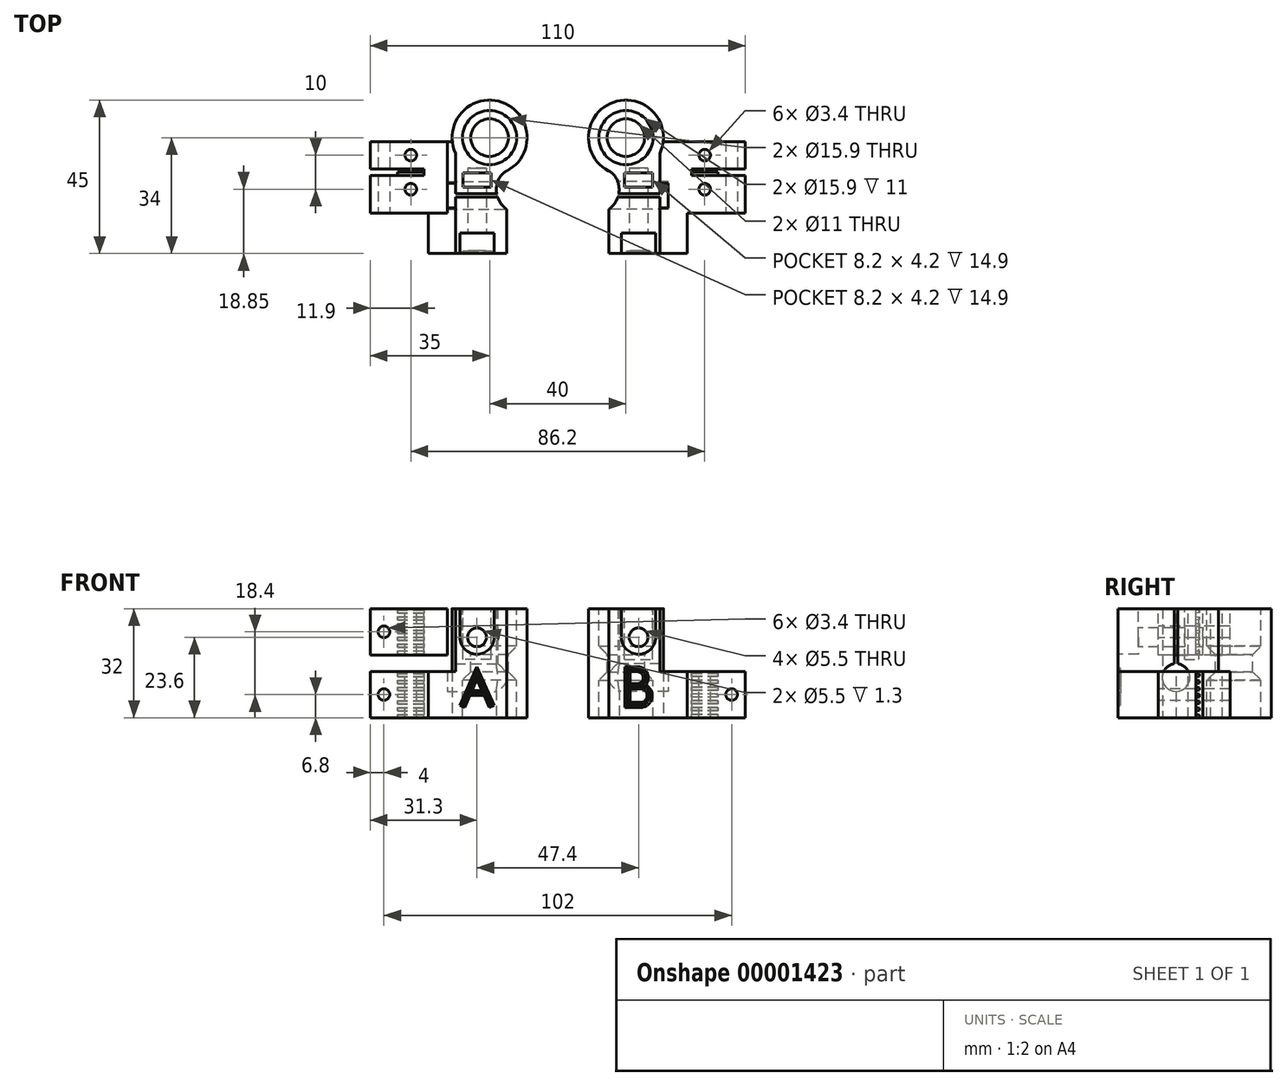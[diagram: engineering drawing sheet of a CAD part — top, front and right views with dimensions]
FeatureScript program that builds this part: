
annotation { "Feature Type Name" : "Feature", "Feature Type Description" : "" }
export const myFeature = defineFeature(function(context is Context, id is Id, definition is map)
    precondition{}
    {
        {
            var Q0;
            Q0=qCreatedBy(makeId("Top.planeOp"),FACE);
            var sketch = newSketch(context, id + "F0", { "sketchPlane" : qUnion([Q0])});
            skArc(sketch, "E0", {"start": v(4.19, -10.17) * mm, "mid": v(5.63, 9.45) * mm, "end": v(-10.94, -1.15) * mm});
            skLineSegment(sketch, "E1", {"start": v(-10.94, -1.15) * mm, "end": v(-35, -1.15) * mm});
            skLineSegment(sketch, "E2", {"start": v(-35, -1.15) * mm, "end": v(-35, -9.15) * mm});
            skLineSegment(sketch, "E3", {"start": v(-35, -9.15) * mm, "end": v(-19.3, -9.15) * mm});
            skLineSegment(sketch, "E4", {"start": v(-19.3, -9.15) * mm, "end": v(-19.3, -11.15) * mm});
            skLineSegment(sketch, "E5", {"start": v(-19.3, -11.15) * mm, "end": v(-35, -11.15) * mm});
            skLineSegment(sketch, "E6", {"start": v(-35, -11.15) * mm, "end": v(-35, -22.15) * mm});
            skLineSegment(sketch, "E7", {"start": v(-35, -22.15) * mm, "end": v(-18, -22.15) * mm});
            skLineSegment(sketch, "E8", {"start": v(-18, -22.15) * mm, "end": v(-18, -34) * mm});
            skLineSegment(sketch, "E9", {"start": v(-18, -34) * mm, "end": v(5, -34) * mm});
            skLineSegment(sketch, "E10", {"start": v(5, -34) * mm, "end": v(5, -21) * mm});
            skArc(sketch, "E11", {"start": v(4.19, -10.17) * mm, "mid": v(2.02, -15.78) * mm, "end": v(5, -21) * mm});
            skSolve(sketch);
        }
        {
            var Q0;
            Q0=makeQuery(id+"F0.imprint","IMPRINT",FACE,{"disambiguationData":[TD([[makeQuery(id+"F0.imprint","IMPRINT",EDGE,{"derivedFrom":sQuery(id+"F0.wireOp",EDGE,"E0")}),1.0]])]});
            extrude(context, id + "F1", {"entities" : qUnion([Q0]), "depth" : 32 * mm});
        }
        {
            var Q0;
            Q0=makeQuery(id+"F1.opExtrude","CAP_FACE",FACE,{"disambiguationData":[OSD([sQuery(id+"F0.wireOp",EDGE,"E0"),sQuery(id+"F0.wireOp",EDGE,"E1"),sQuery(id+"F0.wireOp",EDGE,"E2"),sQuery(id+"F0.wireOp",EDGE,"E3"),sQuery(id+"F0.wireOp",EDGE,"E4"),sQuery(id+"F0.wireOp",EDGE,"E5"),sQuery(id+"F0.wireOp",EDGE,"E6"),sQuery(id+"F0.wireOp",EDGE,"E7"),sQuery(id+"F0.wireOp",EDGE,"E8"),sQuery(id+"F0.wireOp",EDGE,"E9"),sQuery(id+"F0.wireOp",EDGE,"E10"),sQuery(id+"F0.wireOp",EDGE,"E11")])],"isStart":false});
            var sketch = newSketch(context, id + "F2", { "sketchPlane" : qUnion([Q0])});
            skLineSegment(sketch, "E12", {"start": v(-10, -34) * mm, "end": v(-10, -4.58) * mm});
            skArc(sketch, "E13", {"start": v(-10.94, -1.15) * mm, "mid": v(-10.6, -2.9) * mm, "end": v(-10, -4.58) * mm});
            skSolve(sketch);
        }
        {
            var Q0;
            Q0 = qSketchRegion(id + "F2", true);
            var Q1;
            {var subQ1=sQuery(id+"F2.wireOp",EDGE,"E12");Q1=makeQuery(id+"F2.imprint","IMPRINT",FACE,{"disambiguationData":[TD([[makeQuery(id+"F2.imprint","IMPRINT",EDGE,{"derivedFrom":subQ1}),1.0]])]});}
            extrude(context, id + "F3", {"entities" : qUnion([Q0, Q1]), "operationType" : NewBodyOperationType.REMOVE, "oppositeDirection" : true, "depth" : 18.4 * mm});
        }
        {
            var Q0;
            Q0=qCreatedBy(makeId("Front.planeOp"),FACE);
            var sketch = newSketch(context, id + "F4", { "sketchPlane" : qUnion([Q0])});
            skLineSegment(sketch, "E14.0", {"start": v(-11, 32) * mm, "end": v(11, 32) * mm, "construction": true});
            skLineSegment(sketch, "E15.0", {"start": v(-11, 0) * mm, "end": v(11, 0) * mm, "construction": true});
            skLineSegment(sketch, "E16", {"start": v(0, 0) * mm, "end": v(0, 32) * mm});
            skLineSegment(sketch, "E17", {"start": v(0, 32) * mm, "end": v(7.95, 32) * mm, "construction": true});
            skLineSegment(sketch, "E18", {"start": v(7.95, 32) * mm, "end": v(7.95, 21) * mm, "construction": true});
            skLineSegment(sketch, "E19", {"start": v(7.95, 21) * mm, "end": v(5.5, 18.55) * mm, "construction": true});
            skLineSegment(sketch, "E20", {"start": v(5.5, 18.55) * mm, "end": v(5.5, 13.45) * mm, "construction": true});
            skLineSegment(sketch, "E21", {"start": v(5.5, 13.45) * mm, "end": v(7.95, 11) * mm, "construction": true});
            skLineSegment(sketch, "E22", {"start": v(7.95, 11) * mm, "end": v(7.95, 0) * mm, "construction": true});
            skLineSegment(sketch, "E23", {"start": v(7.95, 0) * mm, "end": v(0, 0) * mm, "construction": true});
            skLineSegment(sketch, "E24", {"start": v(-7.95, 0) * mm, "end": v(-7.95, 11) * mm});
            skLineSegment(sketch, "E25", {"start": v(-7.95, 11) * mm, "end": v(-5.5, 13.45) * mm});
            skLineSegment(sketch, "E26", {"start": v(-5.5, 13.45) * mm, "end": v(-5.5, 18.55) * mm});
            skLineSegment(sketch, "E27", {"start": v(-5.5, 18.55) * mm, "end": v(-7.95, 21) * mm});
            skLineSegment(sketch, "E28", {"start": v(-7.95, 21) * mm, "end": v(-7.95, 32) * mm});
            skLineSegment(sketch, "E29", {"start": v(-7.95, 32) * mm, "end": v(0, 32) * mm});
            skLineSegment(sketch, "E30", {"start": v(0, 0) * mm, "end": v(-7.95, 0) * mm});
            skSolve(sketch);
        }
        {
            var Q0;
            Q0=makeQuery(id+"F4.imprint","IMPRINT",FACE,{"disambiguationData":[TD([[makeQuery(id+"F4.imprint","IMPRINT",EDGE,{"derivedFrom":sQuery(id+"F4.wireOp",EDGE,"E16")}),1.0]])]});
            var Q1;
            Q1=sQuery(id+"F4.wireOp",EDGE,"E16");
            revolve(context, id + "F5", {"operationType" : NewBodyOperationType.REMOVE, "entities" : qUnion([Q0]), "axis" : qUnion([Q1]), "revolveType" : RevolveType.FULL, "oppositeDirection" : true});
        }
        {
            var Q0;
            Q0=makeQuery(id+"F1.opExtrude","SWEPT_FACE",FACE,{"disambiguationData":[OSD([sQuery(id+"F0.wireOp",EDGE,"E10")])]});
            var sketch = newSketch(context, id + "F6", { "sketchPlane" : qUnion([Q0])});
            skArc(sketch, "E31", {"start": v(-17.5, 15.82) * mm, "mid": v(-17, 7.75) * mm, "end": v(-16.5, 15.82) * mm});
            skLineSegment(sketch, "E32", {"start": v(-17, 11.8) * mm, "end": v(-17, 32) * mm, "construction": true});
            skLineSegment(sketch, "E33", {"start": v(-17, 32) * mm, "end": v(-17.5, 32) * mm});
            skLineSegment(sketch, "E34", {"start": v(-17.5, 32) * mm, "end": v(-17.5, 15.82) * mm});
            skLineSegment(sketch, "E35", {"start": v(-17.5, 15.82) * mm, "end": v(-16.5, 15.82) * mm, "construction": true});
            skLineSegment(sketch, "E36", {"start": v(-16.5, 15.82) * mm, "end": v(-16.5, 32) * mm});
            skLineSegment(sketch, "E37", {"start": v(-16.5, 32) * mm, "end": v(-17, 32) * mm});
            skSolve(sketch);
        }
        {
            var Q0;
            Q0 = qSketchRegion(id + "F6", true);
            extrude(context, id + "F7", {"entities" : qUnion([Q0]), "operationType" : NewBodyOperationType.REMOVE, "oppositeDirection" : true, "depth" : 17.4 * mm});
        }
        {
            var Q0;
            Q0=makeQuery(id+"F1.opExtrude","SWEPT_FACE",FACE,{"disambiguationData":[OSD([sQuery(id+"F0.wireOp",EDGE,"E9")])]});
            var sketch = newSketch(context, id + "F8", { "sketchPlane" : qUnion([Q0])});
            skCircle(sketch, "E38", {"center": v(-3.7, 23.6) * mm, "radius": 2.75 * mm});
            skSolve(sketch);
        }
        {
            var Q0;
            Q0=makeQuery(id+"F8.imprint","IMPRINT",FACE,{"disambiguationData":[TD([[makeQuery(id+"F8.imprint","IMPRINT",EDGE,{"derivedFrom":sQuery(id+"F8.wireOp",EDGE,"E38")}),1.0]])]});
            var Q1;
            Q1=makeQuery(id+"F5.boolean.opBoolean","COPY",FACE,{"derivedFrom":makeQuery(id+"F5.opRevolve","SWEPT_FACE",FACE,{"disambiguationData":[OSD([sQuery(id+"F4.wireOp",EDGE,"E28")])]})});
            extrude(context, id + "F9", {"entities" : qUnion([Q0]), "operationType" : NewBodyOperationType.REMOVE, "oppositeDirection" : true, "endBoundEntity" : qUnion([Q1]), "depth" : 25 * mm});
        }
        {
            var Q0;
            {var subQ0=sQuery(id+"F0.wireOp",EDGE,"E0");var subQ1=sQuery(id+"F0.wireOp",EDGE,"E11");Q0=makeQuery(id+"F7.boolean.opBoolean","SPLIT",FACE,{"disambiguationData":[TD([makeQuery(id+"F1.opExtrude","SWEPT_FACE",FACE,{"disambiguationData":[OSD([subQ0])]})])],"derivedFrom":makeQuery(id+"F1.opExtrude","CAP_FACE",FACE,{"disambiguationData":[OSD([subQ0,sQuery(id+"F0.wireOp",EDGE,"E1"),sQuery(id+"F0.wireOp",EDGE,"E2"),sQuery(id+"F0.wireOp",EDGE,"E3"),sQuery(id+"F0.wireOp",EDGE,"E4"),sQuery(id+"F0.wireOp",EDGE,"E5"),sQuery(id+"F0.wireOp",EDGE,"E6"),sQuery(id+"F0.wireOp",EDGE,"E7"),sQuery(id+"F0.wireOp",EDGE,"E8"),sQuery(id+"F0.wireOp",EDGE,"E9"),sQuery(id+"F0.wireOp",EDGE,"E10"),subQ1])],"isStart":false})});}
            var sketch = newSketch(context, id + "F10", { "sketchPlane" : qUnion([Q0])});
            skLineSegment(sketch, "E39.0", {"start": v(-0.95, -34) * mm, "end": v(-6.45, -34) * mm, "construction": true});
            skLineSegment(sketch, "E40", {"start": v(-3.7, -34) * mm, "end": v(-3.7, -12.4) * mm, "construction": true});
            skLineSegment(sketch, "E41.rect.bottom", {"start": v(0.4, -14.5) * mm, "end": v(-7.8, -14.5) * mm});
            skLineSegment(sketch, "E41.rect.top", {"start": v(0.4, -10.3) * mm, "end": v(-7.8, -10.3) * mm});
            skLineSegment(sketch, "E41.rect.left", {"start": v(0.4, -14.5) * mm, "end": v(0.4, -10.3) * mm});
            skLineSegment(sketch, "E41.rect.right", {"start": v(-7.8, -14.5) * mm, "end": v(-7.8, -10.3) * mm});
            skPoint(sketch, "E41.rect.middle", {"position": v(-3.7, -12.4) * mm});
            skSolve(sketch);
        }
        {
            var Q0;
            Q0=makeQuery(id+"F10.imprint","IMPRINT",FACE,{"disambiguationData":[TD([[makeQuery(id+"F10.imprint","IMPRINT",EDGE,{"derivedFrom":sQuery(id+"F10.wireOp",EDGE,"E41.rect.bottom")}),-1.0]])]});
            extrude(context, id + "F11", {"entities" : qUnion([Q0]), "operationType" : NewBodyOperationType.REMOVE, "oppositeDirection" : true, "depth" : 14.9 * mm});
        }
        {
            var Q0;
            Q0=makeQuery(id+"F3.boolean.opBoolean","COPY",FACE,{"derivedFrom":makeQuery(id+"F3.opExtrude","CAP_FACE",FACE,{"disambiguationData":[OSD([sQuery(id+"F0.wireOp",EDGE,"E1"),sQuery(id+"F0.wireOp",EDGE,"E2"),sQuery(id+"F0.wireOp",EDGE,"E3"),sQuery(id+"F0.wireOp",EDGE,"E4"),sQuery(id+"F0.wireOp",EDGE,"E5"),sQuery(id+"F0.wireOp",EDGE,"E6"),sQuery(id+"F0.wireOp",EDGE,"E7"),sQuery(id+"F0.wireOp",EDGE,"E8"),sQuery(id+"F0.wireOp",EDGE,"E9"),sQuery(id+"F2.wireOp",EDGE,"E12"),sQuery(id+"F2.wireOp",EDGE,"E13")])],"isStart":false})});
            var sketch = newSketch(context, id + "F12", { "sketchPlane" : qUnion([Q0])});
            skCircle(sketch, "E42", {"center": v(-23.1, -15.15) * mm, "radius": 1.7 * mm});
            skLineSegment(sketch, "E43", {"start": v(-23.1, -15.15) * mm, "end": v(-23.1, -5.15) * mm, "construction": true});
            skCircle(sketch, "E44", {"center": v(-23.1, -5.15) * mm, "radius": 1.7 * mm});
            skSolve(sketch);
        }
        {
            var Q0;
            {Q0=qUnion([makeQuery(id+"F12.imprint","IMPRINT",FACE,{"disambiguationData":[TD([[makeQuery(id+"F12.imprint","IMPRINT",EDGE,{"derivedFrom":sQuery(id+"F12.wireOp",EDGE,"E42")}),1.0]])]}),makeQuery(id+"F12.imprint","IMPRINT",FACE,{"disambiguationData":[TD([[makeQuery(id+"F12.imprint","IMPRINT",EDGE,{"derivedFrom":sQuery(id+"F12.wireOp",EDGE,"E44")}),1.0]])]})]);}
            extrude(context, id + "F13", {"entities" : qUnion([Q0]), "operationType" : NewBodyOperationType.REMOVE, "endBound" : BoundingType.THROUGH_ALL, "oppositeDirection" : true, "depth" : 25 * mm});
        }
        {
            var Q0;
            Q0=makeQuery(id+"F1.opExtrude","SWEPT_FACE",FACE,{"disambiguationData":[OSD([sQuery(id+"F0.wireOp",EDGE,"E7")])]});
            var sketch = newSketch(context, id + "F14", { "sketchPlane" : qUnion([Q0])});
            skLineSegment(sketch, "E45", {"start": v(-35, 6.8) * mm, "end": v(-31, 6.8) * mm, "construction": true});
            skCircle(sketch, "E46", {"center": v(-31, 6.8) * mm, "radius": 1.7 * mm});
            skSolve(sketch);
        }
        {
            var Q0;
            Q0=makeQuery(id+"F14.imprint","IMPRINT",FACE,{"disambiguationData":[TD([[makeQuery(id+"F14.imprint","IMPRINT",EDGE,{"derivedFrom":sQuery(id+"F14.wireOp",EDGE,"E46")}),1.0]])]});
            extrude(context, id + "F15", {"entities" : qUnion([Q0]), "operationType" : NewBodyOperationType.REMOVE, "endBound" : BoundingType.THROUGH_ALL, "oppositeDirection" : true, "depth" : 25 * mm});
        }
        {
            var Q0;
            Q0=makeQuery(id+"F1.opExtrude","SWEPT_FACE",FACE,{"disambiguationData":[OSD([sQuery(id+"F0.wireOp",EDGE,"E9")])]});
            var sketch = newSketch(context, id + "F16", { "sketchPlane" : qUnion([Q0])});
            skArc(sketch, "E47", {"start": v(-8.7, 23.6) * mm, "mid": v(-3.7, 18.6) * mm, "end": v(1.3, 23.6) * mm});
            skLineSegment(sketch, "E48", {"start": v(-8.7, 23.6) * mm, "end": v(-8.7, 32) * mm});
            skLineSegment(sketch, "E49", {"start": v(1.3, 23.6) * mm, "end": v(1.3, 32) * mm});
            skLineSegment(sketch, "E50", {"start": v(1.3, 32) * mm, "end": v(-8.7, 32) * mm});
            skSolve(sketch);
        }
        {
            var Q0;
            {var subQ0=makeQuery(id+"F16.imprint","IMPRINT",EDGE,{"derivedFrom":makeQuery(id+"F9.boolean.opBoolean","COPY",EDGE,{"derivedFrom":makeQuery(id+"F9.opExtrude","CAP_EDGE",EDGE,{"disambiguationData":[OSD([sQuery(id+"F8.wireOp",EDGE,"E38")])],"isStart":true})})});Q0=qUnion([makeQuery(id+"F16.imprint","IMPRINT",FACE,{"disambiguationData":[TD([[subQ0,1.0]])]}),makeQuery(id+"F16.imprint","IMPRINT",FACE,{"disambiguationData":[TD([[makeQuery(id+"F16.imprint","IMPRINT",EDGE,{"derivedFrom":sQuery(id+"F16.wireOp",EDGE,"E47")}),1.0]])]})]);}
            extrude(context, id + "F17", {"entities" : qUnion([Q0]), "operationType" : NewBodyOperationType.REMOVE, "oppositeDirection" : true, "depth" : 6 * mm});
        }
        {
            var Q0;
            Q0=makeQuery(id+"F1.opExtrude","SWEPT_FACE",FACE,{"disambiguationData":[OSD([sQuery(id+"F0.wireOp",EDGE,"E4")])]});
            var sketch = newSketch(context, id + "F18", { "sketchPlane" : qUnion([Q0])});
            skLineSegment(sketch, "E51", {"start": v(11.15, 0) * mm, "end": v(10.15, 0.1) * mm});
            skLineSegment(sketch, "E52", {"start": v(10.15, 0.1) * mm, "end": v(10.15, 0.9) * mm});
            skLineSegment(sketch, "E53", {"start": v(10.15, 0.9) * mm, "end": v(11.15, 1) * mm});
            skLineSegment(sketch, "E54", {"start": v(11.15, 1) * mm, "end": v(11.15, 0) * mm});
            skLineSegment(sketch, "E55", {"start": v(11.15, 1) * mm, "end": v(11.15, 2) * mm, "construction": true});
            skLineSegment(sketch, "E56", {"start": v(11.15, 2) * mm, "end": v(10.15, 2.1) * mm});
            skLineSegment(sketch, "E57", {"start": v(10.15, 2.1) * mm, "end": v(10.15, 2.9) * mm});
            skLineSegment(sketch, "E58", {"start": v(10.15, 2.9) * mm, "end": v(11.15, 3) * mm});
            skLineSegment(sketch, "E59", {"start": v(11.15, 3) * mm, "end": v(11.15, 2) * mm});
            skLineSegment(sketch, "E60", {"start": v(11.15, 3) * mm, "end": v(11.15, 4) * mm});
            skLineSegment(sketch, "E61", {"start": v(11.15, 4) * mm, "end": v(10.15, 4.1) * mm});
            skLineSegment(sketch, "E62", {"start": v(10.15, 4.1) * mm, "end": v(10.15, 4.9) * mm});
            skLineSegment(sketch, "E63", {"start": v(10.15, 4.9) * mm, "end": v(11.15, 5) * mm});
            skLineSegment(sketch, "E64", {"start": v(11.15, 5) * mm, "end": v(11.15, 6) * mm});
            skLineSegment(sketch, "E65", {"start": v(11.15, 6) * mm, "end": v(10.15, 6.1) * mm});
            skLineSegment(sketch, "E66", {"start": v(10.15, 6.1) * mm, "end": v(10.15, 6.9) * mm});
            skLineSegment(sketch, "E67", {"start": v(10.15, 6.9) * mm, "end": v(11.15, 7) * mm});
            skLineSegment(sketch, "E68", {"start": v(11.15, 7) * mm, "end": v(11.15, 6) * mm});
            skLineSegment(sketch, "E69", {"start": v(11.15, 8) * mm, "end": v(10.15, 8.1) * mm});
            skLineSegment(sketch, "E70", {"start": v(10.15, 8.1) * mm, "end": v(10.15, 8.9) * mm});
            skLineSegment(sketch, "E71", {"start": v(10.15, 8.9) * mm, "end": v(11.15, 9) * mm});
            skLineSegment(sketch, "E72", {"start": v(11.15, 9) * mm, "end": v(11.15, 8) * mm});
            skLineSegment(sketch, "E73", {"start": v(11.15, 10) * mm, "end": v(10.15, 10.1) * mm});
            skLineSegment(sketch, "E74", {"start": v(10.15, 10.1) * mm, "end": v(10.15, 10.9) * mm});
            skLineSegment(sketch, "E75", {"start": v(10.15, 10.9) * mm, "end": v(11.15, 11) * mm});
            skLineSegment(sketch, "E76", {"start": v(11.15, 11) * mm, "end": v(11.15, 10) * mm});
            skLineSegment(sketch, "E77", {"start": v(11.15, 12) * mm, "end": v(10.15, 12.1) * mm});
            skLineSegment(sketch, "E78", {"start": v(10.15, 12.1) * mm, "end": v(10.15, 12.9) * mm});
            skLineSegment(sketch, "E79", {"start": v(10.15, 12.9) * mm, "end": v(11.15, 13) * mm});
            skLineSegment(sketch, "E80", {"start": v(11.15, 13) * mm, "end": v(11.15, 12) * mm});
            skLineSegment(sketch, "E81", {"start": v(11.15, 4) * mm, "end": v(11.15, 5) * mm});
            skLineSegment(sketch, "E82", {"start": v(11.15, 7) * mm, "end": v(11.15, 8) * mm, "construction": true});
            skLineSegment(sketch, "E83", {"start": v(11.15, 9) * mm, "end": v(11.15, 10) * mm, "construction": true});
            skLineSegment(sketch, "E84", {"start": v(11.15, 11) * mm, "end": v(11.15, 12) * mm, "construction": true});
            skSolve(sketch);
        }
        {
            var Q0;
            {Q0=qUnion([makeQuery(id+"F18.imprint","IMPRINT",FACE,{"disambiguationData":[TD([[makeQuery(id+"F18.imprint","IMPRINT",EDGE,{"derivedFrom":sQuery(id+"F18.wireOp",EDGE,"E51")}),-1.0]])]}),makeQuery(id+"F18.imprint","IMPRINT",FACE,{"disambiguationData":[TD([[makeQuery(id+"F18.imprint","IMPRINT",EDGE,{"derivedFrom":sQuery(id+"F18.wireOp",EDGE,"E56")}),-1.0]])]}),makeQuery(id+"F18.imprint","IMPRINT",FACE,{"disambiguationData":[TD([[makeQuery(id+"F18.imprint","IMPRINT",EDGE,{"derivedFrom":sQuery(id+"F18.wireOp",EDGE,"E61")}),-1.0]])]}),makeQuery(id+"F18.imprint","IMPRINT",FACE,{"disambiguationData":[TD([[makeQuery(id+"F18.imprint","IMPRINT",EDGE,{"derivedFrom":sQuery(id+"F18.wireOp",EDGE,"E65")}),-1.0]])]}),makeQuery(id+"F18.imprint","IMPRINT",FACE,{"disambiguationData":[TD([[makeQuery(id+"F18.imprint","IMPRINT",EDGE,{"derivedFrom":sQuery(id+"F18.wireOp",EDGE,"E69")}),-1.0]])]}),makeQuery(id+"F18.imprint","IMPRINT",FACE,{"disambiguationData":[TD([[makeQuery(id+"F18.imprint","IMPRINT",EDGE,{"derivedFrom":sQuery(id+"F18.wireOp",EDGE,"E73")}),-1.0]])]}),makeQuery(id+"F18.imprint","IMPRINT",FACE,{"disambiguationData":[TD([[makeQuery(id+"F18.imprint","IMPRINT",EDGE,{"derivedFrom":sQuery(id+"F18.wireOp",EDGE,"E77")}),-1.0]])]})]);}
            extrude(context, id + "F19", {"entities" : qUnion([Q0]), "operationType" : NewBodyOperationType.ADD, "depth" : 7.7 * mm});
        }
        {
            var Q0;
            Q0=makeQuery(id+"F1.opExtrude","SWEPT_EDGE",EDGE,{"disambiguationData":[OSD([sQuery(id+"F0.wireOp",EDGE,"E0"),sQuery(id+"F0.wireOp",EDGE,"E11")])]});
            fillet(context, id + "F20", {"entities" : qUnion([Q0]), "radius" : 5 * mm, "tangentPropagation" : true, "allowEdgeOverflow" : false});
        }
        {
            var Q0;
            Q0=qCreatedBy(makeId("Right.planeOp"),FACE);
            cPlane(context, id + "F21", {"entities" : qUnion([Q0]), "cplaneType" : CPlaneType.OFFSET, "offset" : 20 * mm, "width" : 150 * mm, "height" : 150 * mm});
        }
        {
            var Q0;
            Q0=makeQuery(id+"F1.opExtrude","SWEPT_BODY",BODY,{"disambiguationData":[OSD([sQuery(id+"F0.wireOp",EDGE,"E0"),sQuery(id+"F0.wireOp",EDGE,"E1"),sQuery(id+"F0.wireOp",EDGE,"E2"),sQuery(id+"F0.wireOp",EDGE,"E3"),sQuery(id+"F0.wireOp",EDGE,"E4"),sQuery(id+"F0.wireOp",EDGE,"E5"),sQuery(id+"F0.wireOp",EDGE,"E6"),sQuery(id+"F0.wireOp",EDGE,"E7"),sQuery(id+"F0.wireOp",EDGE,"E8"),sQuery(id+"F0.wireOp",EDGE,"E9"),sQuery(id+"F0.wireOp",EDGE,"E10"),sQuery(id+"F0.wireOp",EDGE,"E11")])]});
            var Q1;
            Q1=qCreatedBy(id+"F21.planeOp",FACE);
            mirror(context, id + "F22", {"entities" : qUnion([Q0]), "mirrorPlane" : qUnion([Q1])});
        }
        {
            var Q0;
            Q0=makeQuery(id+"F1.opExtrude","SWEPT_FACE",FACE,{"disambiguationData":[OSD([sQuery(id+"F0.wireOp",EDGE,"E9")])]});
            var sketch = newSketch(context, id + "F23", { "sketchPlane" : qUnion([Q0])});
            skLineSegment(sketch, "E85", {"start": v(-3.7, 18.6) * mm, "end": v(-3.7, 0) * mm, "construction": true});
            skLineSegment(sketch, "E86", {"start": v(-3.7, 15) * mm, "end": v(-8.7, 3.6) * mm});
            skLineSegment(sketch, "E87", {"start": v(-8.7, 3.6) * mm, "end": v(-7.33, 3) * mm});
            skLineSegment(sketch, "E88", {"start": v(-7.33, 3) * mm, "end": v(-5.8, 6.5) * mm});
            skLineSegment(sketch, "E89", {"start": v(-5.8, 6.5) * mm, "end": v(-3.7, 6.5) * mm});
            skLineSegment(sketch, "E90", {"start": v(-3.7, 6.5) * mm, "end": v(-1.6, 6.5) * mm});
            skLineSegment(sketch, "E91", {"start": v(-1.6, 6.5) * mm, "end": v(-0.07, 3) * mm});
            skLineSegment(sketch, "E92", {"start": v(-0.07, 3) * mm, "end": v(1.3, 3.6) * mm});
            skLineSegment(sketch, "E93", {"start": v(1.3, 3.6) * mm, "end": v(-3.7, 15) * mm});
            skLineSegment(sketch, "E94", {"start": v(-7.33, 3) * mm, "end": v(-0.07, 3) * mm, "construction": true});
            skLineSegment(sketch, "E95", {"start": v(-3.7, 11.27) * mm, "end": v(-5.13, 8) * mm});
            skLineSegment(sketch, "E96", {"start": v(-5.13, 8) * mm, "end": v(-2.27, 8) * mm});
            skLineSegment(sketch, "E97", {"start": v(-2.27, 8) * mm, "end": v(-3.7, 11.27) * mm});
            skLineSegment(sketch, "E98", {"start": v(-5.8, 6.5) * mm, "end": v(-5.13, 8) * mm, "construction": true});
            skLineSegment(sketch, "E99", {"start": v(-2.27, 8) * mm, "end": v(-1.6, 6.5) * mm, "construction": true});
            skSolve(sketch);
        }
        {
            var Q0;
            Q0=makeQuery(id+"F23.imprint","IMPRINT",FACE,{"disambiguationData":[TD([[makeQuery(id+"F23.imprint","IMPRINT",EDGE,{"derivedFrom":sQuery(id+"F23.wireOp",EDGE,"E86")}),1.0]])]});
            extrude(context, id + "F24", {"entities" : qUnion([Q0]), "operationType" : NewBodyOperationType.REMOVE, "oppositeDirection" : true, "depth" : .75 * mm});
        }
        {
            var Q0;
            Q0=makeQuery(id+"F24.boolean.opBoolean","COPY",FACE,{"derivedFrom":makeQuery(id+"F24.opExtrude","CAP_FACE",FACE,{"disambiguationData":[OSD([sQuery(id+"F23.wireOp",EDGE,"E86"),sQuery(id+"F23.wireOp",EDGE,"E87"),sQuery(id+"F23.wireOp",EDGE,"E88"),sQuery(id+"F23.wireOp",EDGE,"E89"),sQuery(id+"F23.wireOp",EDGE,"E90"),sQuery(id+"F23.wireOp",EDGE,"E91"),sQuery(id+"F23.wireOp",EDGE,"E92"),sQuery(id+"F23.wireOp",EDGE,"E93"),sQuery(id+"F23.wireOp",EDGE,"E95"),sQuery(id+"F23.wireOp",EDGE,"E96"),sQuery(id+"F23.wireOp",EDGE,"E97")])],"isStart":false})});
            chamfer(context, id + "F25", {"entities" : qUnion([Q0]), "width" : .75 * mm, "tangentPropagation" : true});
        }
        {
            var Q0;
            Q0=makeQuery(id+"F22.opPattern","COPY",FACE,{"derivedFrom":makeQuery(id+"F1.opExtrude","SWEPT_FACE",FACE,{"disambiguationData":[OSD([sQuery(id+"F0.wireOp",EDGE,"E9")])]}),"instanceName":"1"});
            var sketch = newSketch(context, id + "F26", { "sketchPlane" : qUnion([Q0])});
            skLineSegment(sketch, "E100", {"start": v(41.2, 13.5) * mm, "end": v(41.2, 10) * mm});
            skLineSegment(sketch, "E101", {"start": v(41.2, 4.5) * mm, "end": v(44.2, 4.5) * mm});
            skArc(sketch, "E102", {"start": v(44.2, 4.5) * mm, "mid": v(46.2, 6.5) * mm, "end": v(44.2, 8.5) * mm});
            skLineSegment(sketch, "E103", {"start": v(41.2, 13.5) * mm, "end": v(43.3, 13.5) * mm});
            skArc(sketch, "E104", {"start": v(43.3, 13.5) * mm, "mid": v(45.05, 11.75) * mm, "end": v(43.3, 10) * mm});
            skArc(sketch, "E105.0", {"start": v(44.2, 3) * mm, "mid": v(47.6, 5.7) * mm, "end": v(45.76, 9.63) * mm});
            skLineSegment(sketch, "E105.1", {"start": v(39.7, 3) * mm, "end": v(44.2, 3) * mm});
            skLineSegment(sketch, "E105.2", {"start": v(39.7, 15) * mm, "end": v(39.7, 3) * mm});
            skLineSegment(sketch, "E105.3", {"start": v(39.7, 15) * mm, "end": v(43.3, 15) * mm});
            skArc(sketch, "E105.4", {"start": v(43.3, 15) * mm, "mid": v(46.25, 13.1) * mm, "end": v(45.76, 9.63) * mm});
            skLineSegment(sketch, "E106", {"start": v(43.3, 10) * mm, "end": v(41.2, 10) * mm});
            skLineSegment(sketch, "E107", {"start": v(44.2, 8.5) * mm, "end": v(41.2, 8.5) * mm});
            skLineSegment(sketch, "E108.trimOffspring", {"start": v(41.2, 8.5) * mm, "end": v(41.2, 4.5) * mm});
            skLineSegment(sketch, "E109", {"start": v(47.7, 6.5) * mm, "end": v(39.7, 6.5) * mm, "construction": true});
            skLineSegment(sketch, "E110", {"start": v(43.7, 6.5) * mm, "end": v(43.7, 18.6) * mm, "construction": true});
            skSolve(sketch);
        }
        {
            var Q0;
            Q0=makeQuery(id+"F26.imprint","IMPRINT",FACE,{"disambiguationData":[TD([[makeQuery(id+"F26.imprint","IMPRINT",EDGE,{"derivedFrom":sQuery(id+"F26.wireOp",EDGE,"E100")}),-1.0]])]});
            extrude(context, id + "F27", {"entities" : qUnion([Q0]), "operationType" : NewBodyOperationType.REMOVE, "oppositeDirection" : true, "depth" : .75 * mm});
        }
        {
            var Q0;
            Q0=makeQuery(id+"F27.boolean.opBoolean","COPY",EDGE,{"derivedFrom":makeQuery(id+"F27.opExtrude","SWEPT_EDGE",EDGE,{"disambiguationData":[OSD([sQuery(id+"F26.wireOp",EDGE,"E105.0"),sQuery(id+"F26.wireOp",EDGE,"E105.4")])]})});
            fillet(context, id + "F28", {"entities" : qUnion([Q0]), "radius" : .1 * mm, "tangentPropagation" : true, "allowEdgeOverflow" : false});
        }
        {
            var Q0;
            Q0=makeQuery(id+"F27.boolean.opBoolean","COPY",FACE,{"derivedFrom":makeQuery(id+"F27.opExtrude","CAP_FACE",FACE,{"disambiguationData":[OSD([sQuery(id+"F26.wireOp",EDGE,"E100"),sQuery(id+"F26.wireOp",EDGE,"E101"),sQuery(id+"F26.wireOp",EDGE,"E102"),sQuery(id+"F26.wireOp",EDGE,"E103"),sQuery(id+"F26.wireOp",EDGE,"E104"),sQuery(id+"F26.wireOp",EDGE,"E105.0"),sQuery(id+"F26.wireOp",EDGE,"E105.1"),sQuery(id+"F26.wireOp",EDGE,"E105.2"),sQuery(id+"F26.wireOp",EDGE,"E105.3"),sQuery(id+"F26.wireOp",EDGE,"E105.4"),sQuery(id+"F26.wireOp",EDGE,"E106"),sQuery(id+"F26.wireOp",EDGE,"E107"),sQuery(id+"F26.wireOp",EDGE,"E108.trimOffspring")])],"isStart":false})});
            chamfer(context, id + "F29", {"entities" : qUnion([Q0]), "width" : .75 * mm, "tangentPropagation" : true});
        }
        {
            var Q0;
            {var subQ0=sQuery(id+"F0.wireOp",EDGE,"E9");var subQ1=sQuery(id+"F0.wireOp",EDGE,"E10");var subQ2=sQuery(id+"F0.wireOp",EDGE,"E11");Q0=makeQuery(id+"F7.boolean.opBoolean","SPLIT",FACE,{"disambiguationData":[TD([makeQuery(id+"F1.opExtrude","SWEPT_FACE",FACE,{"disambiguationData":[OSD([subQ0])]})])],"derivedFrom":makeQuery(id+"F1.opExtrude","CAP_FACE",FACE,{"disambiguationData":[OSD([sQuery(id+"F0.wireOp",EDGE,"E0"),sQuery(id+"F0.wireOp",EDGE,"E1"),sQuery(id+"F0.wireOp",EDGE,"E2"),sQuery(id+"F0.wireOp",EDGE,"E3"),sQuery(id+"F0.wireOp",EDGE,"E4"),sQuery(id+"F0.wireOp",EDGE,"E5"),sQuery(id+"F0.wireOp",EDGE,"E6"),sQuery(id+"F0.wireOp",EDGE,"E7"),sQuery(id+"F0.wireOp",EDGE,"E8"),subQ0,subQ1,subQ2])],"isStart":false})});}
            cPlane(context, id + "F30", {"entities" : qUnion([Q0]), "cplaneType" : CPlaneType.OFFSET, "offset" : 0 * mm, "width" : 150 * mm, "height" : 150 * mm});
        }
        {
            var Q0;
            Q0=qCreatedBy(id+"F30.planeOp",FACE);
            var sketch = newSketch(context, id + "F31", { "sketchPlane" : qUnion([Q0])});
            skLineSegment(sketch, "E111.0", {"start": v(-35, -11.15) * mm, "end": v(-35, -22.15) * mm});
            skLineSegment(sketch, "E111.1", {"start": v(-19.3, -11.15) * mm, "end": v(-35, -11.15) * mm});
            skLineSegment(sketch, "E111.2", {"start": v(-35, -9.15) * mm, "end": v(-19.3, -9.15) * mm});
            skLineSegment(sketch, "E111.3", {"start": v(-19.3, -9.15) * mm, "end": v(-19.3, -11.15) * mm});
            skLineSegment(sketch, "E111.4", {"start": v(-35, -1.15) * mm, "end": v(-35, -9.15) * mm});
            skLineSegment(sketch, "E112", {"start": v(-35, -1.15) * mm, "end": v(-12.4, -1.15) * mm});
            skLineSegment(sketch, "E113", {"start": v(-12.4, -1.15) * mm, "end": v(-12.4, -22.15) * mm});
            skLineSegment(sketch, "E114", {"start": v(-12.4, -22.15) * mm, "end": v(-35, -22.15) * mm});
            skSolve(sketch);
        }
        {
            var Q0;
            Q0=makeQuery(id+"F31.imprint","IMPRINT",FACE,{"disambiguationData":[TD([[makeQuery(id+"F31.imprint","IMPRINT",EDGE,{"derivedFrom":sQuery(id+"F31.wireOp",EDGE,"E111.0")}),1.0]])]});
            extrude(context, id + "F32", {"entities" : qUnion([Q0]), "oppositeDirection" : true, "depth" : 13.6 * mm});
        }
        {
            var Q0;
            Q0=makeQuery(id+"F32.opExtrude","CAP_FACE",FACE,{"disambiguationData":[OSD([sQuery(id+"F31.wireOp",EDGE,"E111.0"),sQuery(id+"F31.wireOp",EDGE,"E111.1"),sQuery(id+"F31.wireOp",EDGE,"E111.2"),sQuery(id+"F31.wireOp",EDGE,"E111.3"),sQuery(id+"F31.wireOp",EDGE,"E111.4"),sQuery(id+"F31.wireOp",EDGE,"E112"),sQuery(id+"F31.wireOp",EDGE,"E113"),sQuery(id+"F31.wireOp",EDGE,"E114")])],"isStart":true});
            var sketch = newSketch(context, id + "F33", { "sketchPlane" : qUnion([Q0])});
            skCircle(sketch, "E115.0", {"center": v(-23.1, -15.15) * mm, "radius": 1.7 * mm});
            skCircle(sketch, "E116.0", {"center": v(-23.1, -5.15) * mm, "radius": 1.7 * mm});
            skSolve(sketch);
        }
        {
            var Q0;
            {Q0=qUnion([makeQuery(id+"F33.imprint","IMPRINT",FACE,{"disambiguationData":[TD([[makeQuery(id+"F33.imprint","IMPRINT",EDGE,{"derivedFrom":sQuery(id+"F33.wireOp",EDGE,"E115.0")}),1.0]])]}),makeQuery(id+"F33.imprint","IMPRINT",FACE,{"disambiguationData":[TD([[makeQuery(id+"F33.imprint","IMPRINT",EDGE,{"derivedFrom":sQuery(id+"F33.wireOp",EDGE,"E116.0")}),1.0]])]})]);}
            extrude(context, id + "F34", {"entities" : qUnion([Q0]), "operationType" : NewBodyOperationType.REMOVE, "endBound" : BoundingType.THROUGH_ALL, "oppositeDirection" : true, "depth" : 25 * mm});
        }
        {
            var Q0;
            Q0=makeQuery(id+"F32.opExtrude","SWEPT_FACE",FACE,{"disambiguationData":[OSD([sQuery(id+"F31.wireOp",EDGE,"E114")])]});
            var sketch = newSketch(context, id + "F35", { "sketchPlane" : qUnion([Q0])});
            skLineSegment(sketch, "E117", {"start": v(-35, 25.2) * mm, "end": v(-31, 25.2) * mm, "construction": true});
            skCircle(sketch, "E118", {"center": v(-31, 25.2) * mm, "radius": 1.7 * mm});
            skSolve(sketch);
        }
        {
            var Q0;
            Q0=makeQuery(id+"F35.imprint","IMPRINT",FACE,{"disambiguationData":[TD([[makeQuery(id+"F35.imprint","IMPRINT",EDGE,{"derivedFrom":sQuery(id+"F35.wireOp",EDGE,"E118")}),1.0]])]});
            extrude(context, id + "F36", {"entities" : qUnion([Q0]), "operationType" : NewBodyOperationType.REMOVE, "endBound" : BoundingType.THROUGH_ALL, "oppositeDirection" : true, "depth" : 25 * mm});
        }
        {
            var Q0;
            Q0=makeQuery(id+"F32.opExtrude","SWEPT_FACE",FACE,{"disambiguationData":[OSD([sQuery(id+"F31.wireOp",EDGE,"E111.3")])]});
            var sketch = newSketch(context, id + "F37", { "sketchPlane" : qUnion([Q0])});
            skLineSegment(sketch, "E119", {"start": v(11.15, 31.7) * mm, "end": v(10.15, 31.6) * mm});
            skLineSegment(sketch, "E120", {"start": v(10.15, 31.6) * mm, "end": v(10.15, 30.8) * mm});
            skLineSegment(sketch, "E121", {"start": v(10.15, 30.8) * mm, "end": v(11.15, 30.7) * mm});
            skLineSegment(sketch, "E122", {"start": v(11.15, 30.7) * mm, "end": v(11.15, 31.7) * mm});
            skLineSegment(sketch, "E123", {"start": v(11.15, 29.7) * mm, "end": v(10.15, 29.6) * mm});
            skLineSegment(sketch, "E124", {"start": v(10.15, 29.6) * mm, "end": v(10.15, 28.8) * mm});
            skLineSegment(sketch, "E125", {"start": v(10.15, 28.8) * mm, "end": v(11.15, 28.7) * mm});
            skLineSegment(sketch, "E126", {"start": v(11.15, 28.7) * mm, "end": v(11.15, 29.7) * mm});
            skLineSegment(sketch, "E127", {"start": v(11.15, 27.7) * mm, "end": v(10.15, 27.6) * mm});
            skLineSegment(sketch, "E128", {"start": v(10.15, 27.6) * mm, "end": v(10.15, 26.8) * mm});
            skLineSegment(sketch, "E129", {"start": v(10.15, 26.8) * mm, "end": v(11.15, 26.7) * mm});
            skLineSegment(sketch, "E130", {"start": v(11.15, 26.7) * mm, "end": v(11.15, 27.7) * mm});
            skLineSegment(sketch, "E131", {"start": v(11.15, 25.7) * mm, "end": v(10.15, 25.6) * mm});
            skLineSegment(sketch, "E132", {"start": v(10.15, 25.6) * mm, "end": v(10.15, 24.8) * mm});
            skLineSegment(sketch, "E133", {"start": v(10.15, 24.8) * mm, "end": v(11.15, 24.7) * mm});
            skLineSegment(sketch, "E134", {"start": v(11.15, 24.7) * mm, "end": v(11.15, 25.7) * mm});
            skLineSegment(sketch, "E135", {"start": v(11.15, 23.7) * mm, "end": v(10.15, 23.6) * mm});
            skLineSegment(sketch, "E136", {"start": v(10.15, 23.6) * mm, "end": v(10.15, 22.8) * mm});
            skLineSegment(sketch, "E137", {"start": v(10.15, 22.8) * mm, "end": v(11.15, 22.7) * mm});
            skLineSegment(sketch, "E138", {"start": v(11.15, 22.7) * mm, "end": v(11.15, 23.7) * mm});
            skLineSegment(sketch, "E139", {"start": v(11.15, 21.7) * mm, "end": v(10.15, 21.6) * mm});
            skLineSegment(sketch, "E140", {"start": v(10.15, 21.6) * mm, "end": v(10.15, 20.8) * mm});
            skLineSegment(sketch, "E141", {"start": v(10.15, 20.8) * mm, "end": v(11.15, 20.7) * mm});
            skLineSegment(sketch, "E142", {"start": v(11.15, 20.7) * mm, "end": v(11.15, 21.7) * mm});
            skLineSegment(sketch, "E143", {"start": v(11.15, 19.7) * mm, "end": v(10.15, 19.6) * mm});
            skLineSegment(sketch, "E144", {"start": v(10.15, 19.6) * mm, "end": v(10.15, 18.8) * mm});
            skLineSegment(sketch, "E145", {"start": v(10.15, 18.8) * mm, "end": v(11.15, 18.7) * mm});
            skLineSegment(sketch, "E146", {"start": v(11.15, 18.7) * mm, "end": v(11.15, 19.7) * mm});
            skLineSegment(sketch, "E147", {"start": v(11.15, 19.7) * mm, "end": v(11.15, 20.7) * mm, "construction": true});
            skLineSegment(sketch, "E148", {"start": v(11.15, 21.7) * mm, "end": v(11.15, 22.7) * mm, "construction": true});
            skLineSegment(sketch, "E149", {"start": v(11.15, 23.7) * mm, "end": v(11.15, 24.7) * mm, "construction": true});
            skLineSegment(sketch, "E150", {"start": v(11.15, 25.7) * mm, "end": v(11.15, 26.7) * mm, "construction": true});
            skLineSegment(sketch, "E151", {"start": v(11.15, 27.7) * mm, "end": v(11.15, 28.7) * mm, "construction": true});
            skLineSegment(sketch, "E152", {"start": v(11.15, 29.7) * mm, "end": v(11.15, 30.7) * mm, "construction": true});
            skLineSegment(sketch, "E153", {"start": v(11.15, 18.7) * mm, "end": v(11.15, 18.4) * mm, "construction": true});
            skLineSegment(sketch, "E154", {"start": v(11.15, 31.7) * mm, "end": v(11.15, 32) * mm, "construction": true});
            skLineSegment(sketch, "E155", {"start": v(9.15, 25.2) * mm, "end": v(10.15, 25.2) * mm, "construction": true});
            skSolve(sketch);
        }
        {
            var Q0;
            {Q0=qUnion([makeQuery(id+"F37.imprint","IMPRINT",FACE,{"disambiguationData":[TD([[makeQuery(id+"F37.imprint","IMPRINT",EDGE,{"derivedFrom":sQuery(id+"F37.wireOp",EDGE,"E119")}),1.0]])]}),makeQuery(id+"F37.imprint","IMPRINT",FACE,{"disambiguationData":[TD([[makeQuery(id+"F37.imprint","IMPRINT",EDGE,{"derivedFrom":sQuery(id+"F37.wireOp",EDGE,"E123")}),1.0]])]}),makeQuery(id+"F37.imprint","IMPRINT",FACE,{"disambiguationData":[TD([[makeQuery(id+"F37.imprint","IMPRINT",EDGE,{"derivedFrom":sQuery(id+"F37.wireOp",EDGE,"E127")}),1.0]])]}),makeQuery(id+"F37.imprint","IMPRINT",FACE,{"disambiguationData":[TD([[makeQuery(id+"F37.imprint","IMPRINT",EDGE,{"derivedFrom":sQuery(id+"F37.wireOp",EDGE,"E131")}),1.0]])]}),makeQuery(id+"F37.imprint","IMPRINT",FACE,{"disambiguationData":[TD([[makeQuery(id+"F37.imprint","IMPRINT",EDGE,{"derivedFrom":sQuery(id+"F37.wireOp",EDGE,"E135")}),1.0]])]}),makeQuery(id+"F37.imprint","IMPRINT",FACE,{"disambiguationData":[TD([[makeQuery(id+"F37.imprint","IMPRINT",EDGE,{"derivedFrom":sQuery(id+"F37.wireOp",EDGE,"E139")}),1.0]])]}),makeQuery(id+"F37.imprint","IMPRINT",FACE,{"disambiguationData":[TD([[makeQuery(id+"F37.imprint","IMPRINT",EDGE,{"derivedFrom":sQuery(id+"F37.wireOp",EDGE,"E143")}),1.0]])]})]);}
            var Q1;
            Q1=makeQuery(id+"F19.opExtrude","CAP_FACE",FACE,{"disambiguationData":[OSD([sQuery(id+"F18.wireOp",EDGE,"E65"),sQuery(id+"F18.wireOp",EDGE,"E66"),sQuery(id+"F18.wireOp",EDGE,"E67"),sQuery(id+"F18.wireOp",EDGE,"E68")])],"isStart":false});
            extrude(context, id + "F38", {"entities" : qUnion([Q0]), "operationType" : NewBodyOperationType.ADD, "endBound" : BoundingType.UP_TO_SURFACE, "endBoundEntityFace" : qUnion([Q1]), "depth" : 25 * mm});
        }
    });
